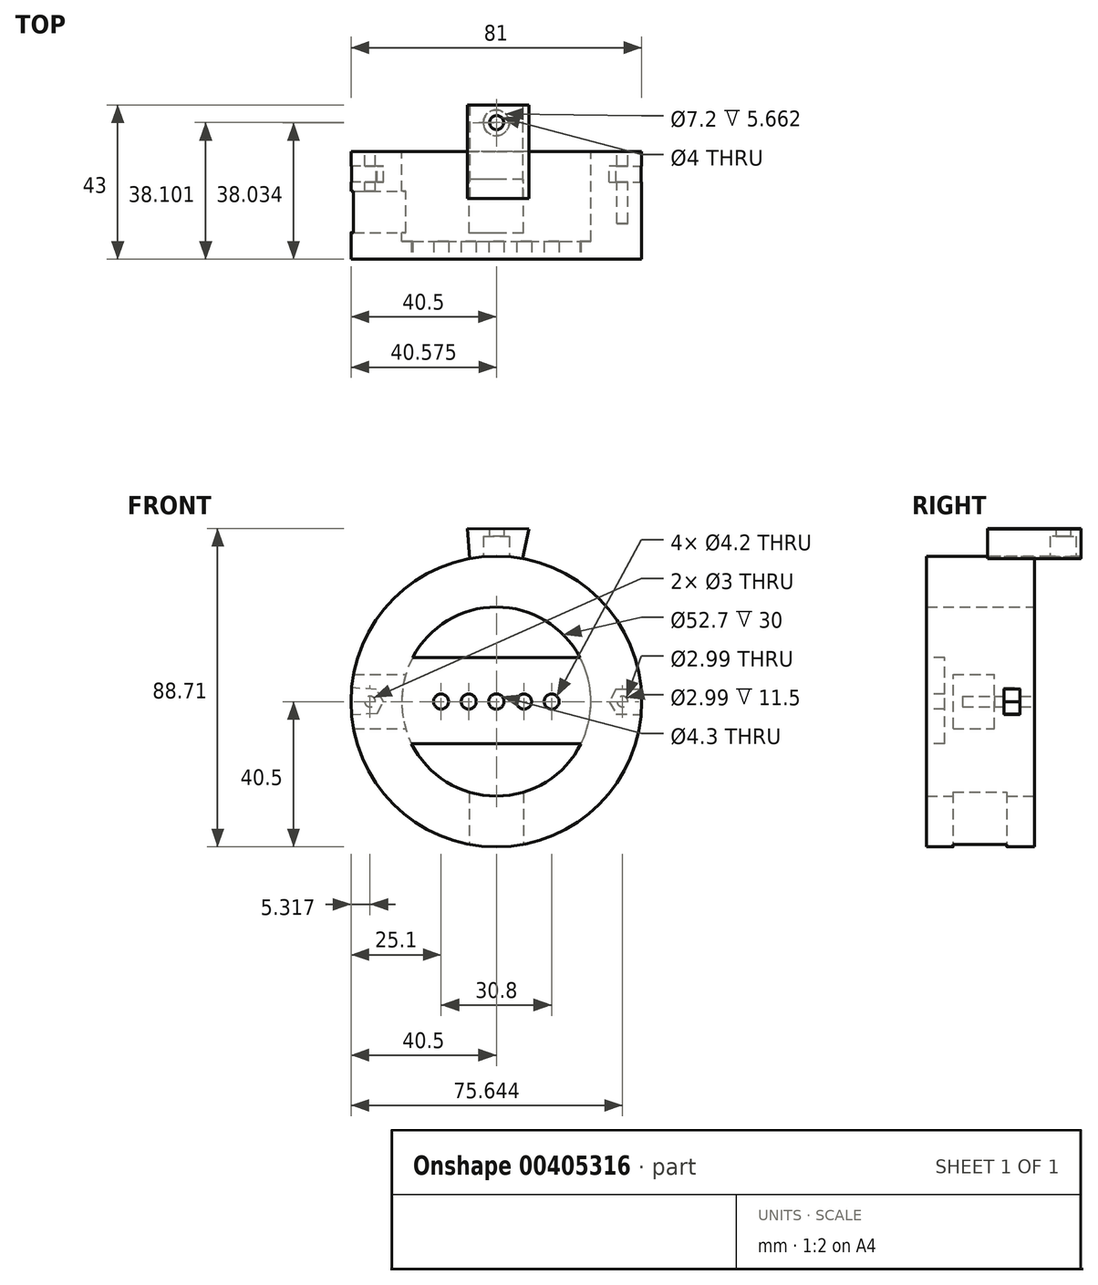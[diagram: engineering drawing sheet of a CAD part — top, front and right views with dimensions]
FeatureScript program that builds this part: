
annotation { "Feature Type Name" : "Feature", "Feature Type Description" : "" }
export const myFeature = defineFeature(function(context is Context, id is Id, definition is map)
    precondition{}
    {
        {
            var Q0;
            Q0=qCreatedBy(makeId("Front.planeOp"),FACE);
            var sketch = newSketch(context, id + "F0", { "sketchPlane" : qUnion([Q0])});
            skCircle(sketch, "E0", {"center": v(0, 0) * mm, "radius": 26.35 * mm});
            skCircle(sketch, "E1", {"center": v(0, 0) * mm, "radius": 40.5 * mm});
            skSolve(sketch);
        }
        {
            var Q0;
            Q0=makeQuery(id+"F0.imprint","IMPRINT",FACE,{"disambiguationData":[TD([[makeQuery(id+"F0.imprint","IMPRINT",EDGE,{"derivedFrom":sQuery(id+"F0.wireOp",EDGE,"E0")}),-1.0]])]});
            extrude(context, id + "F1", {"entities" : qUnion([Q0]), "depth" : 30 * mm});
        }
        {
            var Q0;
            Q0=makeQuery(id+"F1.opExtrude","CAP_FACE",FACE,{"disambiguationData":[OSD([sQuery(id+"F0.wireOp",EDGE,"E0"),sQuery(id+"F0.wireOp",EDGE,"E1")])],"isStart":true});
            var sketch = newSketch(context, id + "F2", { "sketchPlane" : qUnion([Q0])});
            skLineSegment(sketch, "E2.3", {"start": v(33.21, -3.3) * mm, "end": v(31.44, -0.05) * mm});
            skLineSegment(sketch, "E2.4", {"start": v(31.44, -0.05) * mm, "end": v(33.4, 3.35) * mm});
            skLineSegment(sketch, "E3.0", {"start": v(-31.43, -0.05) * mm, "end": v(-33.4, -3.45) * mm});
            skLineSegment(sketch, "E3.5", {"start": v(-33.4, 3.45) * mm, "end": v(-31.43, -0.05) * mm});
            skLineSegment(sketch, "E4", {"start": v(-33.4, -3.45) * mm, "end": v(-40.34, -3.61) * mm});
            skLineSegment(sketch, "E5", {"start": v(-33.4, 3.45) * mm, "end": v(-40.35, 3.52) * mm});
            skLineSegment(sketch, "E6", {"start": v(33.21, -3.3) * mm, "end": v(40.33, -3.72) * mm});
            skLineSegment(sketch, "E7", {"start": v(33.4, 3.35) * mm, "end": v(40.32, 3.85) * mm});
            skSolve(sketch);
        }
        {
            var Q0;
            Q0=makeQuery(id+"F2.imprint","IMPRINT",FACE,{"disambiguationData":[TD([[makeQuery(id+"F2.imprint","IMPRINT",EDGE,{"derivedFrom":sQuery(id+"F2.wireOp",EDGE,"E2.3")}),1.0]])]});
            var sketch = newSketch(context, id + "F3", { "sketchPlane" : qUnion([Q0])});
            skCircle(sketch, "E8", {"center": v(35.18, 0) * mm, "radius": 1.5 * mm});
            skCircle(sketch, "E9", {"center": v(-35.14, 0) * mm, "radius": 1.5 * mm});
            skSolve(sketch);
        }
        {
            var Q0;
            Q0 = qSketchRegion(id + "F3", true);
            extrude(context, id + "F4", {"entities" : qUnion([Q0]), "operationType" : NewBodyOperationType.REMOVE, "oppositeDirection" : true, "depth" : 20 * mm});
        }
        {
            var Q0;
            Q0=makeQuery(id+"F2.imprint","IMPRINT",FACE,{"disambiguationData":[TD([[makeQuery(id+"F2.imprint","IMPRINT",EDGE,{"derivedFrom":sQuery(id+"F2.wireOp",EDGE,"E2.3")}),-1.0]])]});
            var Q1;
            Q1=makeQuery(id+"F2.imprint","IMPRINT",FACE,{"disambiguationData":[TD([[makeQuery(id+"F2.imprint","IMPRINT",EDGE,{"derivedFrom":sQuery(id+"F2.wireOp",EDGE,"E3.0")}),-1.0]])]});
            extrude(context, id + "F5", {"entities" : qUnion([Q0, Q1]), "oppositeDirection" : true, "depth" : 4.5 * mm});
        }
        {
            var Q0;
            Q0=makeQuery(id+"F5.opExtrude","SWEPT_BODY",BODY,{"disambiguationData":[OSD([sQuery(id+"F0.wireOp",EDGE,"E1"),sQuery(id+"F2.wireOp",EDGE,"E2.3"),sQuery(id+"F2.wireOp",EDGE,"E2.4"),sQuery(id+"F2.wireOp",EDGE,"E6"),sQuery(id+"F2.wireOp",EDGE,"E7")])]});
            var Q1;
            Q1=makeQuery(id+"F5.opExtrude","SWEPT_BODY",BODY,{"disambiguationData":[OSD([sQuery(id+"F0.wireOp",EDGE,"E1"),sQuery(id+"F2.wireOp",EDGE,"E3.0"),sQuery(id+"F2.wireOp",EDGE,"E3.5"),sQuery(id+"F2.wireOp",EDGE,"E4"),sQuery(id+"F2.wireOp",EDGE,"E5")])]});
            transform(context, id + "F6", {"entities" : qUnion([Q0, Q1]), "transformType" : TransformType.TRANSLATION_3D, "dx" : 0 * mm, "dy" : -4 * mm, "dz" : 0 * mm, "makeCopy" : false});
        }
        {
            var Q0;
            Q0=makeQuery(id+"F5.opExtrude","SWEPT_BODY",BODY,{"disambiguationData":[OSD([sQuery(id+"F0.wireOp",EDGE,"E1"),sQuery(id+"F2.wireOp",EDGE,"E3.0"),sQuery(id+"F2.wireOp",EDGE,"E3.5"),sQuery(id+"F2.wireOp",EDGE,"E4"),sQuery(id+"F2.wireOp",EDGE,"E5")])]});
            var Q1;
            Q1=makeQuery(id+"F5.opExtrude","SWEPT_BODY",BODY,{"disambiguationData":[OSD([sQuery(id+"F0.wireOp",EDGE,"E1"),sQuery(id+"F2.wireOp",EDGE,"E2.3"),sQuery(id+"F2.wireOp",EDGE,"E2.4"),sQuery(id+"F2.wireOp",EDGE,"E6"),sQuery(id+"F2.wireOp",EDGE,"E7")])]});
            var Q2;
            Q2=makeQuery(id+"F1.opExtrude","SWEPT_BODY",BODY,{"disambiguationData":[OSD([sQuery(id+"F0.wireOp",EDGE,"E0"),sQuery(id+"F0.wireOp",EDGE,"E1")])]});
            booleanBodies(context, id + "F7", {"operationType" : BooleanOperationType.SUBTRACTION, "tools" : qUnion([Q0, Q1]), "targets" : qUnion([Q2])});
        }
        {
            var Q0;
            Q0=makeQuery(id+"F1.opExtrude","CAP_FACE",FACE,{"disambiguationData":[OSD([sQuery(id+"F0.wireOp",EDGE,"E0"),sQuery(id+"F0.wireOp",EDGE,"E1")])],"isStart":false});
            var sketch = newSketch(context, id + "F8", { "sketchPlane" : qUnion([Q0])});
            skLineSegment(sketch, "E10.bottom", {"start": v(-38.58, 12.31) * mm, "end": v(38.78, 12.31) * mm});
            skLineSegment(sketch, "E10.top", {"start": v(-38.58, -11.69) * mm, "end": v(38.78, -11.69) * mm});
            skLineSegment(sketch, "E10.left", {"start": v(-38.58, 12.31) * mm, "end": v(-38.58, -11.69) * mm});
            skLineSegment(sketch, "E10.right", {"start": v(38.78, 12.31) * mm, "end": v(38.78, -11.69) * mm});
            skCircle(sketch, "E11", {"center": v(0, 0) * mm, "radius": 2.15 * mm});
            skCircle(sketch, "E12", {"center": v(-7.7, 0) * mm, "radius": 2.1 * mm});
            skCircle(sketch, "E13", {"center": v(7.7, 0) * mm, "radius": 2.1 * mm});
            skLineSegment(sketch, "E14", {"start": v(0, 0) * mm, "end": v(7.7, 0) * mm});
            skLineSegment(sketch, "E15", {"start": v(0, 0) * mm, "end": v(-7.7, 0) * mm});
            skCircle(sketch, "E16", {"center": v(-15.4, 0) * mm, "radius": 2.1 * mm});
            skCircle(sketch, "E17", {"center": v(15.4, 0) * mm, "radius": 2.1 * mm});
            skLineSegment(sketch, "E18", {"start": v(-7.7, 0) * mm, "end": v(-15.4, 0) * mm});
            skLineSegment(sketch, "E19", {"start": v(7.7, 0) * mm, "end": v(15.4, 0) * mm});
            skSolve(sketch);
        }
        {
            var Q0;
            Q0=makeQuery(id+"F8.imprint","IMPRINT",FACE,{"disambiguationData":[TD([[makeQuery(id+"F8.imprint","IMPRINT",EDGE,{"derivedFrom":sQuery(id+"F8.wireOp",EDGE,"E16")}),-1.0]])]});
            extrude(context, id + "F9", {"entities" : qUnion([Q0]), "operationType" : NewBodyOperationType.ADD, "oppositeDirection" : true, "depth" : 5 * mm});
        }
        {
            var Q0;
            Q0=qCreatedBy(makeId("Right.planeOp"),FACE);
            var sketch = newSketch(context, id + "F10", { "sketchPlane" : qUnion([Q0])});
            skLineSegment(sketch, "E20", {"start": v(0, -38.82) * mm, "end": v(-15, -38.82) * mm});
            skLineSegment(sketch, "E21.bottom", {"start": v(-7.66, -23.01) * mm, "end": v(-22.66, -23.01) * mm});
            skLineSegment(sketch, "E21.top", {"start": v(-7.66, -43.01) * mm, "end": v(-22.66, -43.01) * mm});
            skLineSegment(sketch, "E21.left", {"start": v(-7.66, -23.01) * mm, "end": v(-7.66, -43.01) * mm});
            skLineSegment(sketch, "E21.right", {"start": v(-22.66, -23.01) * mm, "end": v(-22.66, -43.01) * mm});
            skSolve(sketch);
        }
        {
            var Q0;
            {var subQ0=sQuery(id+"F10.wireOp",EDGE,"E21.bottom");Q0=makeQuery(id+"F10.imprint","IMPRINT",FACE,{"disambiguationData":[TD([[makeQuery(id+"F10.imprint","IMPRINT",EDGE,{"derivedFrom":subQ0}),1.0]])]});}
            extrude(context, id + "F11", {"entities" : qUnion([Q0]), "operationType" : NewBodyOperationType.REMOVE, "depth" : 15 * mm, "symmetric" : true});
        }
        {
            var Q0;
            Q0=qCreatedBy(makeId("Top.planeOp"),FACE);
            var sketch = newSketch(context, id + "F12", { "sketchPlane" : qUnion([Q0])});
            skLineSegment(sketch, "E22.bottom", {"start": v(-43.95, -11.07) * mm, "end": v(-23.95, -11.07) * mm});
            skLineSegment(sketch, "E22.top", {"start": v(-43.95, -22.57) * mm, "end": v(-23.95, -22.57) * mm});
            skLineSegment(sketch, "E22.left", {"start": v(-43.95, -11.07) * mm, "end": v(-43.95, -22.57) * mm});
            skLineSegment(sketch, "E22.right", {"start": v(-23.95, -11.07) * mm, "end": v(-23.95, -22.57) * mm});
            skLineSegment(sketch, "E23.bottom", {"start": v(-43.95, -11.07) * mm, "end": v(-43.95, -12.56) * mm});
            skSolve(sketch);
        }
        {
            var Q0;
            Q0 = qSketchRegion(id + "F12", true);
            extrude(context, id + "F13", {"entities" : qUnion([Q0]), "operationType" : NewBodyOperationType.REMOVE, "depth" : 15 * mm, "symmetric" : true});
        }
        {
            var Q0;
            Q0=makeQuery(id+"F1.opExtrude","CAP_FACE",FACE,{"disambiguationData":[OSD([sQuery(id+"F0.wireOp",EDGE,"E0"),sQuery(id+"F0.wireOp",EDGE,"E1")])],"isStart":true});
            var sketch = newSketch(context, id + "F14", { "sketchPlane" : qUnion([Q0])});
            skLineSegment(sketch, "E24", {"start": v(8.09, 48.21) * mm, "end": v(7.39, 39.82) * mm});
            skLineSegment(sketch, "E25", {"start": v(-9.14, 48.14) * mm, "end": v(-7.32, 39.83) * mm});
            skLineSegment(sketch, "E26", {"start": v(-9.14, 48.14) * mm, "end": v(8.09, 48.21) * mm});
            skSolve(sketch);
        }
        {
            var Q0;
            {var subQ0=sQuery(id+"F14.wireOp",EDGE,"E24");Q0=makeQuery(id+"F14.imprint","IMPRINT",FACE,{"disambiguationData":[TD([[makeQuery(id+"F14.imprint","IMPRINT",EDGE,{"derivedFrom":subQ0}),-1.0]])]});}
            extrude(context, id + "F15", {"entities" : qUnion([Q0]), "depth" : 26 * mm, "symmetric" : true});
        }
        {
            var Q0;
            Q0=qCreatedBy(makeId("Top.planeOp"),FACE);
            var sketch = newSketch(context, id + "F16", { "sketchPlane" : qUnion([Q0])});
            skCircle(sketch, "E27", {"center": v(0, 8.03) * mm, "radius": 3.6 * mm});
            skSolve(sketch);
        }
        {
            var Q0;
            Q0=makeQuery(id+"F16.imprint","IMPRINT",FACE,{"disambiguationData":[TD([[makeQuery(id+"F16.imprint","IMPRINT",EDGE,{"derivedFrom":sQuery(id+"F16.wireOp",EDGE,"E27")}),1.0]])]});
            extrude(context, id + "F17", {"entities" : qUnion([Q0]), "operationType" : NewBodyOperationType.REMOVE, "depth" : 46 * mm});
        }
        {
            var Q0;
            Q0=qCreatedBy(makeId("Top.planeOp"),FACE);
            var sketch = newSketch(context, id + "F18", { "sketchPlane" : qUnion([Q0])});
            skCircle(sketch, "E28", {"center": v(0.08, 8.1) * mm, "radius": 2 * mm});
            skSolve(sketch);
        }
        {
            var Q0;
            Q0=makeQuery(id+"F18.imprint","IMPRINT",FACE,{"disambiguationData":[TD([[makeQuery(id+"F18.imprint","IMPRINT",EDGE,{"derivedFrom":sQuery(id+"F18.wireOp",EDGE,"E28")}),1.0]])]});
            extrude(context, id + "F19", {"entities" : qUnion([Q0]), "operationType" : NewBodyOperationType.REMOVE, "depth" : 56.1 * mm});
        }
    });
